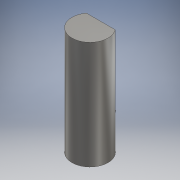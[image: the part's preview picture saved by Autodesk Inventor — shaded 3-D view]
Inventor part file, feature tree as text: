
AUTODESK INVENTOR PART (.ipt)
format: ipt  version: 2018 (Build 220112000, 112)  size: 105,984 bytes
history: native  units: mm
features: extrude x2, sketch x2, plane x1, projected_geometry x1
ambient origin geometry x8: Origin, YZ Plane, XZ Plane, XY Plane, X Axis, Y Axis, Z Axis, Center Point
bodies: Solid1 (feature_tree)
feature tree (6):
  extrude  "Extrusion1"  Depth=15.0mm TaperAngle=0.0deg
  plane  "Work Plane2"
  extrude  "Extrusion2"  Depth=10.0mm
  sketch  "Sketch1"  dims[d0=5.0mm d1=15.0mm d2=0.0mm]
  sketch  "Sketch2"  dims[d5=1.0mm d6=10.0mm d7=15.0mm d8=0.0mm]
  projected_geometry  "Projected Loop1"
